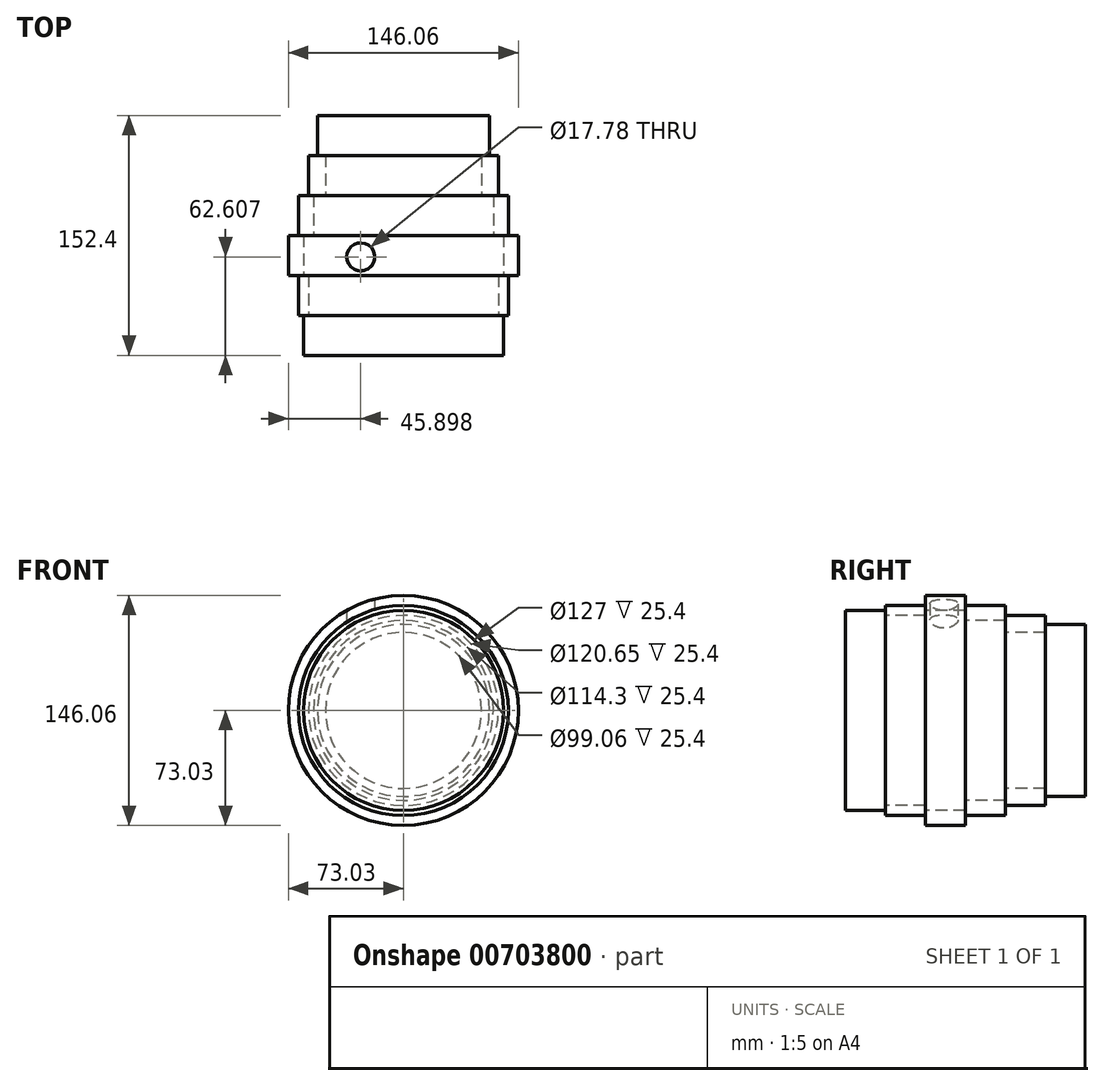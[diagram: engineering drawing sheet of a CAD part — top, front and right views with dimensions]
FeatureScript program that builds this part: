
annotation { "Feature Type Name" : "Feature", "Feature Type Description" : "" }
export const myFeature = defineFeature(function(context is Context, id is Id, definition is map)
    precondition{}
    {
        {
            var Q0;
            Q0=qCreatedBy(makeId("Front.planeOp"),FACE);
            var sketch = newSketch(context, id + "F0", { "sketchPlane" : qUnion([Q0])});
            skCircle(sketch, "E0", {"center": v(0, 0) * mm, "radius": 63.5 * mm});
            skSolve(sketch);
        }
        {
            var Q0;
            Q0=makeQuery(id+"F0.imprint","IMPRINT",FACE,{"disambiguationData":[TD([[makeQuery(id+"F0.imprint","IMPRINT",EDGE,{"derivedFrom":sQuery(id+"F0.wireOp",EDGE,"E0")}),1.0]])]});
            extrude(context, id + "F1", {"entities" : qUnion([Q0]), "depth" : 25.4 * mm, "offsetDistance" : 25.4 * mm});
        }
        {
            var Q0;
            Q0=makeQuery(id+"F1.opExtrude","CAP_FACE",FACE,{"disambiguationData":[OSD([sQuery(id+"F0.wireOp",EDGE,"E0")])],"isStart":true});
            var sketch = newSketch(context, id + "F2", { "sketchPlane" : qUnion([Q0])});
            skCircle(sketch, "E1", {"center": v(0, 0) * mm, "radius": 66.68 * mm});
            skCircle(sketch, "E2", {"center": v(0, 0) * mm, "radius": 60.32 * mm});
            skSolve(sketch);
        }
        {
            var Q0;
            Q0 = qSketchRegion(id + "F2", true);
            extrude(context, id + "F3", {"entities" : qUnion([Q0]), "operationType" : NewBodyOperationType.ADD, "depth" : 25.4 * mm, "offsetDistance" : 25.4 * mm});
        }
        {
            var Q0;
            Q0=makeQuery(id+"F3.opExtrude","CAP_FACE",FACE,{"disambiguationData":[OSD([sQuery(id+"F2.wireOp",EDGE,"E1"),sQuery(id+"F2.wireOp",EDGE,"E2")])],"isStart":false});
            var sketch = newSketch(context, id + "F4", { "sketchPlane" : qUnion([Q0])});
            skCircle(sketch, "E3", {"center": v(0, 0) * mm, "radius": 73.03 * mm});
            skCircle(sketch, "E4", {"center": v(0, 0) * mm, "radius": 63.5 * mm});
            skSolve(sketch);
        }
        {
            var Q0;
            Q0 = qSketchRegion(id + "F4", true);
            extrude(context, id + "F5", {"entities" : qUnion([Q0]), "operationType" : NewBodyOperationType.ADD, "depth" : 25.4 * mm, "offsetDistance" : 25.4 * mm});
        }
        {
            var Q0;
            Q0=makeQuery(id+"F5.opExtrude","CAP_FACE",FACE,{"disambiguationData":[OSD([sQuery(id+"F4.wireOp",EDGE,"E3"),sQuery(id+"F4.wireOp",EDGE,"E4")])],"isStart":false});
            var sketch = newSketch(context, id + "F6", { "sketchPlane" : qUnion([Q0])});
            skCircle(sketch, "E5", {"center": v(0, 0) * mm, "radius": 66.68 * mm});
            skCircle(sketch, "E6", {"center": v(0, 0) * mm, "radius": 57.15 * mm});
            skSolve(sketch);
        }
        {
            var Q0;
            Q0 = qSketchRegion(id + "F6", true);
            extrude(context, id + "F7", {"entities" : qUnion([Q0]), "operationType" : NewBodyOperationType.ADD, "depth" : 25.4 * mm, "offsetDistance" : 25.4 * mm});
        }
        {
            var Q0;
            Q0=makeQuery(id+"F7.opExtrude","CAP_FACE",FACE,{"disambiguationData":[OSD([sQuery(id+"F6.wireOp",EDGE,"E5"),sQuery(id+"F6.wireOp",EDGE,"E6")])],"isStart":false});
            var sketch = newSketch(context, id + "F8", { "sketchPlane" : qUnion([Q0])});
            skCircle(sketch, "E7", {"center": v(0, 0) * mm, "radius": 60.33 * mm});
            skCircle(sketch, "E8", {"center": v(0, 0) * mm, "radius": 49.53 * mm});
            skSolve(sketch);
        }
        {
            var Q0;
            Q0 = qSketchRegion(id + "F8", true);
            extrude(context, id + "F9", {"entities" : qUnion([Q0]), "operationType" : NewBodyOperationType.ADD, "depth" : 25.4 * mm, "offsetDistance" : 25.4 * mm});
        }
        {
            var Q0;
            Q0=makeQuery(id+"F9.opExtrude","CAP_FACE",FACE,{"disambiguationData":[OSD([sQuery(id+"F8.wireOp",EDGE,"E7"),sQuery(id+"F8.wireOp",EDGE,"E8")])],"isStart":false});
            var sketch = newSketch(context, id + "F10", { "sketchPlane" : qUnion([Q0])});
            skCircle(sketch, "E9", {"center": v(0, 0) * mm, "radius": 54.61 * mm});
            skSolve(sketch);
        }
        {
            var Q0;
            Q0 = qSketchRegion(id + "F10", true);
            extrude(context, id + "F11", {"entities" : qUnion([Q0]), "operationType" : NewBodyOperationType.ADD, "depth" : 25.4 * mm, "offsetDistance" : 25.4 * mm});
        }
        {
            var Q0;
            Q0=qCreatedBy(makeId("Top.planeOp"),FACE);
            var sketch = newSketch(context, id + "F12", { "sketchPlane" : qUnion([Q0])});
            skPoint(sketch, "E10", {"position": v(-27.13, 37.2) * mm});
            skPoint(sketch, "E11", {"position": v(-27.13, 29.7) * mm});
            skSolve(sketch);
        }
        {
            var Q0;
            Q0=sQuery(id+"F12.wireOp",VERTEX,"E10");
            var Q1;
            Q1=makeQuery(id+"F1.opExtrude","SWEPT_BODY",BODY,{"disambiguationData":[OSD([sQuery(id+"F0.wireOp",EDGE,"E0")])]});
            hole(context, id + "F13", {"style" : HoleStyle.SIMPLE, "endStyle" : HoleEndStyle.THROUGH, "oppositeDirection" : true, "holeDiameter" : 17.78 * mm, "majorDiameter" : 6.35 * mm, "isTappedThrough" : true, "tappedDepth" : 12.7 * mm, "tapClearance" : 3, "locations" : qUnion([Q0]), "scope" : qUnion([Q1])});
        }
    });
